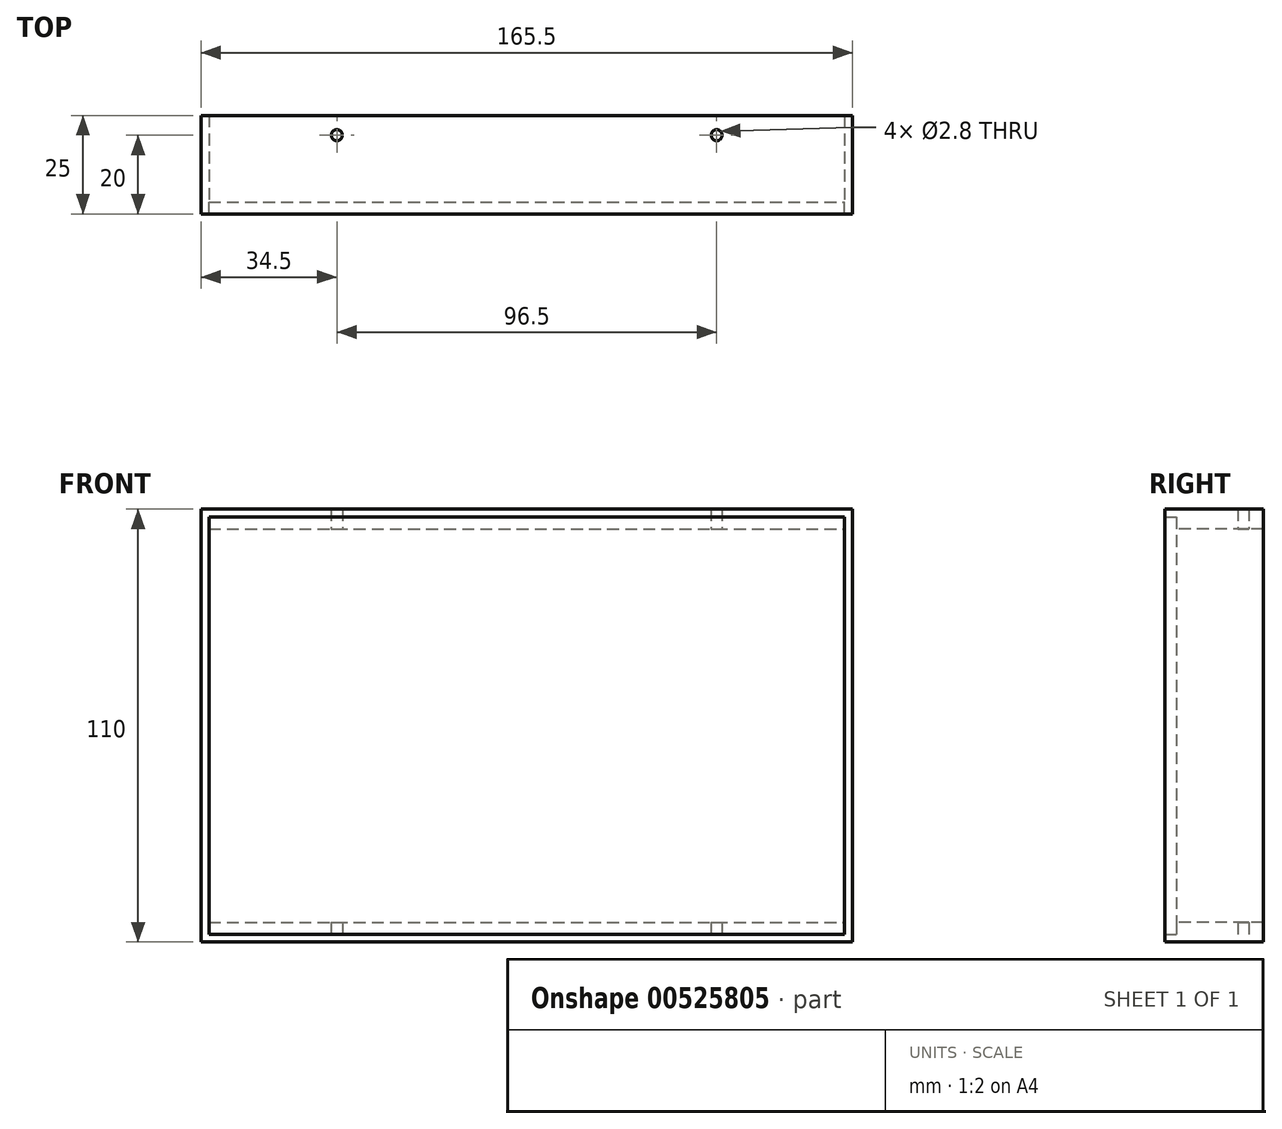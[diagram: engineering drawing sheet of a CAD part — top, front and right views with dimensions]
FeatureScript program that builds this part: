
annotation { "Feature Type Name" : "Feature", "Feature Type Description" : "" }
export const myFeature = defineFeature(function(context is Context, id is Id, definition is map)
    precondition{}
    {
        {
            var Q0;
            Q0=qCreatedBy(makeId("Front.planeOp"),FACE);
            var sketch = newSketch(context, id + "F0", { "sketchPlane" : qUnion([Q0])});
            skLineSegment(sketch, "E0.bottom", {"start": v(75.25, -46.75) * mm, "end": v(-75.25, -46.75) * mm});
            skLineSegment(sketch, "E0.top", {"start": v(75.25, 46.75) * mm, "end": v(-75.25, 46.75) * mm});
            skLineSegment(sketch, "E0.left", {"start": v(75.25, -46.75) * mm, "end": v(75.25, 46.75) * mm});
            skLineSegment(sketch, "E0.right", {"start": v(-75.25, -46.75) * mm, "end": v(-75.25, 46.75) * mm});
            skPoint(sketch, "E0.middle", {"position": v(0, 0) * mm});
            skLineSegment(sketch, "E1.bottom", {"start": v(-81.75, 50.75) * mm, "end": v(79.75, 50.75) * mm});
            skLineSegment(sketch, "E1.top", {"start": v(-81.75, -55.25) * mm, "end": v(79.75, -55.25) * mm});
            skLineSegment(sketch, "E1.left", {"start": v(-81.75, 50.75) * mm, "end": v(-81.75, -55.25) * mm});
            skLineSegment(sketch, "E1.right", {"start": v(79.75, 50.75) * mm, "end": v(79.75, -55.25) * mm});
            skSolve(sketch);
        }
        {
            var Q0;
            Q0=qCreatedBy(makeId("Front.planeOp"),FACE);
            var sketch = newSketch(context, id + "F1", { "sketchPlane" : qUnion([Q0])});
            skLineSegment(sketch, "E2.bottom", {"start": v(-81.75, 50.75) * mm, "end": v(79.75, 50.75) * mm});
            skLineSegment(sketch, "E2.top", {"start": v(-81.75, -55.25) * mm, "end": v(79.75, -55.25) * mm});
            skLineSegment(sketch, "E2.left", {"start": v(-81.75, 50.75) * mm, "end": v(-81.75, -55.25) * mm});
            skLineSegment(sketch, "E2.right", {"start": v(79.75, 50.75) * mm, "end": v(79.75, -55.25) * mm});
            skLineSegment(sketch, "E3.bottom", {"start": v(-83.75, 52.75) * mm, "end": v(81.75, 52.75) * mm});
            skLineSegment(sketch, "E3.top", {"start": v(-83.75, -57.25) * mm, "end": v(81.75, -57.25) * mm});
            skLineSegment(sketch, "E3.left", {"start": v(-83.75, 52.75) * mm, "end": v(-83.75, -57.25) * mm});
            skLineSegment(sketch, "E3.right", {"start": v(81.75, 52.75) * mm, "end": v(81.75, -57.25) * mm});
            skSolve(sketch);
        }
        {
            var Q0;
            Q0=qSketchRegion(id+"F1",true);
            extrude(context, id + "F2", {"entities" : qUnion([Q0]), "depth" : 3 * mm});
        }
        {
            var Q0;
            Q0=qCreatedBy(makeId("Front.planeOp"),FACE);
            var sketch = newSketch(context, id + "F3", { "sketchPlane" : qUnion([Q0])});
            skLineSegment(sketch, "E4.bottom", {"start": v(-83.75, 52.75) * mm, "end": v(81.75, 52.75) * mm});
            skLineSegment(sketch, "E4.top", {"start": v(-83.75, -57.25) * mm, "end": v(81.75, -57.25) * mm});
            skLineSegment(sketch, "E4.left", {"start": v(-83.75, 52.75) * mm, "end": v(-83.75, -57.25) * mm});
            skLineSegment(sketch, "E4.right", {"start": v(81.75, 52.75) * mm, "end": v(81.75, -57.25) * mm});
            skLineSegment(sketch, "E5.bottom", {"start": v(-81.75, 47.75) * mm, "end": v(79.75, 47.75) * mm});
            skLineSegment(sketch, "E5.top", {"start": v(-81.75, -52.25) * mm, "end": v(79.75, -52.25) * mm});
            skLineSegment(sketch, "E5.left", {"start": v(-81.75, 47.75) * mm, "end": v(-81.75, -52.25) * mm});
            skLineSegment(sketch, "E5.right", {"start": v(79.75, 47.75) * mm, "end": v(79.75, -52.25) * mm});
            skSolve(sketch);
        }
        {
            var Q0;
            Q0=qSketchRegion(id+"F3",true);
            extrude(context, id + "F4", {"entities" : qUnion([Q0]), "operationType" : NewBodyOperationType.ADD, "oppositeDirection" : true, "depth" : 22 * mm});
        }
        {
            var Q0;
            Q0=makeQuery(id+"F4.boolean.opBoolean","MERGE",FACE,{"derivedFrom":[makeQuery(id+"F2.opExtrude","SWEPT_FACE",FACE,{"disambiguationData":[OSD([sQuery(id+"F1.wireOp",EDGE,"E3.top")])]}),makeQuery(id+"F4.opExtrude","SWEPT_FACE",FACE,{"disambiguationData":[OSD([sQuery(id+"F3.wireOp",EDGE,"E4.top")])]})]});
            var sketch = newSketch(context, id + "F5", { "sketchPlane" : qUnion([Q0])});
            skCircle(sketch, "E6", {"center": v(-49.25, -17) * mm, "radius": 1.4 * mm});
            skCircle(sketch, "E7", {"center": v(47.25, -17) * mm, "radius": 1.4 * mm});
            skSolve(sketch);
        }
        {
            var Q0;
            Q0=qSketchRegion(id+"F5",true);
            extrude(context, id + "F6", {"entities" : qUnion([Q0]), "operationType" : NewBodyOperationType.REMOVE, "endBound" : BoundingType.THROUGH_ALL, "oppositeDirection" : true, "depth" : 25 * mm});
        }
        {
            var Q0;
            Q0=qCreatedBy(makeId("Front.planeOp"),FACE);
            var sketch = newSketch(context, id + "F7", { "sketchPlane" : qUnion([Q0])});
            skLineSegment(sketch, "E8.bottom", {"start": v(-81.75, 50.75) * mm, "end": v(79.75, 50.75) * mm});
            skLineSegment(sketch, "E8.top", {"start": v(-81.75, -55.25) * mm, "end": v(79.75, -55.25) * mm});
            skLineSegment(sketch, "E8.left", {"start": v(-81.75, 50.75) * mm, "end": v(-81.75, -55.25) * mm});
            skLineSegment(sketch, "E8.right", {"start": v(79.75, 50.75) * mm, "end": v(79.75, -55.25) * mm});
            skSolve(sketch);
        }
        {
            var Q0;
            Q0=qSketchRegion(id+"F7",true);
            extrude(context, id + "F8", {"entities" : qUnion([Q0]), "depth" : 3 * mm});
        }
    });
